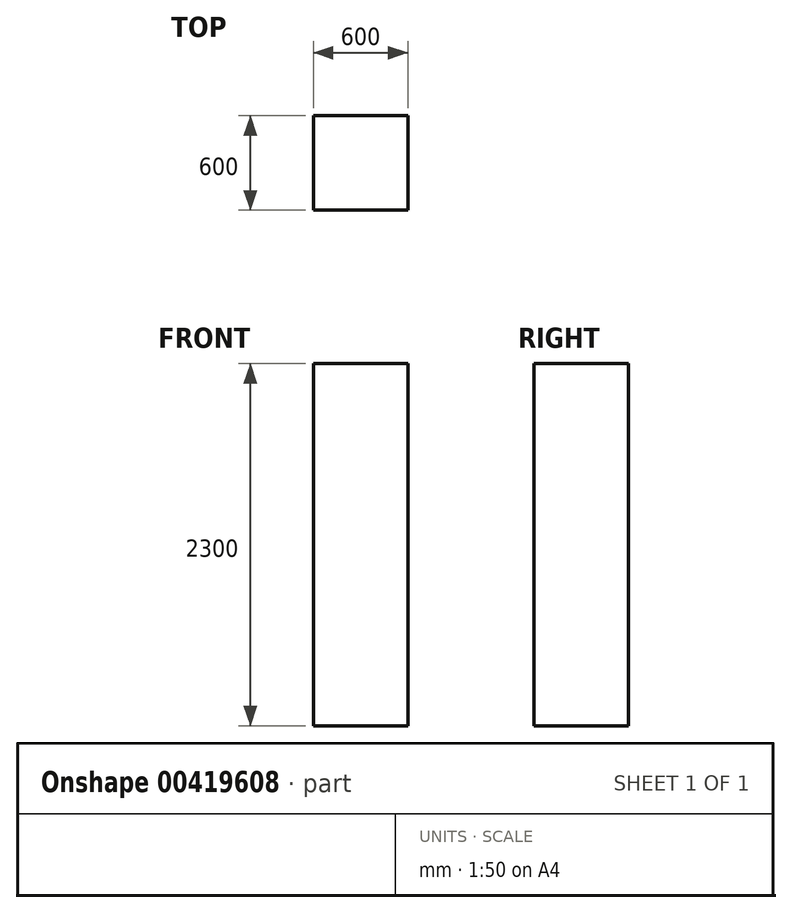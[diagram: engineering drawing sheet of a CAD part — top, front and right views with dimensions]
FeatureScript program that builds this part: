
annotation { "Feature Type Name" : "Feature", "Feature Type Description" : "" }
export const myFeature = defineFeature(function(context is Context, id is Id, definition is map)
    precondition{}
    {
        {
            var Q0;
            Q0=qCreatedBy(makeId("Top.planeOp"),FACE);
            var sketch = newSketch(context, id + "F0", { "sketchPlane" : qUnion([Q0])});
            skLineSegment(sketch, "E0.bottom", {"start": v(-531.85, 495.43) * mm, "end": v(68.15, 495.43) * mm});
            skLineSegment(sketch, "E0.top", {"start": v(-531.85, -104.57) * mm, "end": v(68.15, -104.57) * mm});
            skLineSegment(sketch, "E0.left", {"start": v(-531.85, 495.43) * mm, "end": v(-531.85, -104.57) * mm});
            skLineSegment(sketch, "E0.right", {"start": v(68.15, 495.43) * mm, "end": v(68.15, -104.57) * mm});
            skSolve(sketch);
        }
        {
            var Q0;
            Q0=makeQuery(id+"F0.imprint","IMPRINT",FACE,{"disambiguationData":[TD([[makeQuery(id+"F0.imprint","IMPRINT",EDGE,{"derivedFrom":sQuery(id+"F0.wireOp",EDGE,"E0.bottom")}),-1.0]])]});
            extrude(context, id + "F1", {"entities" : qUnion([Q0]), "depth" : 2300 * mm});
        }
    });
